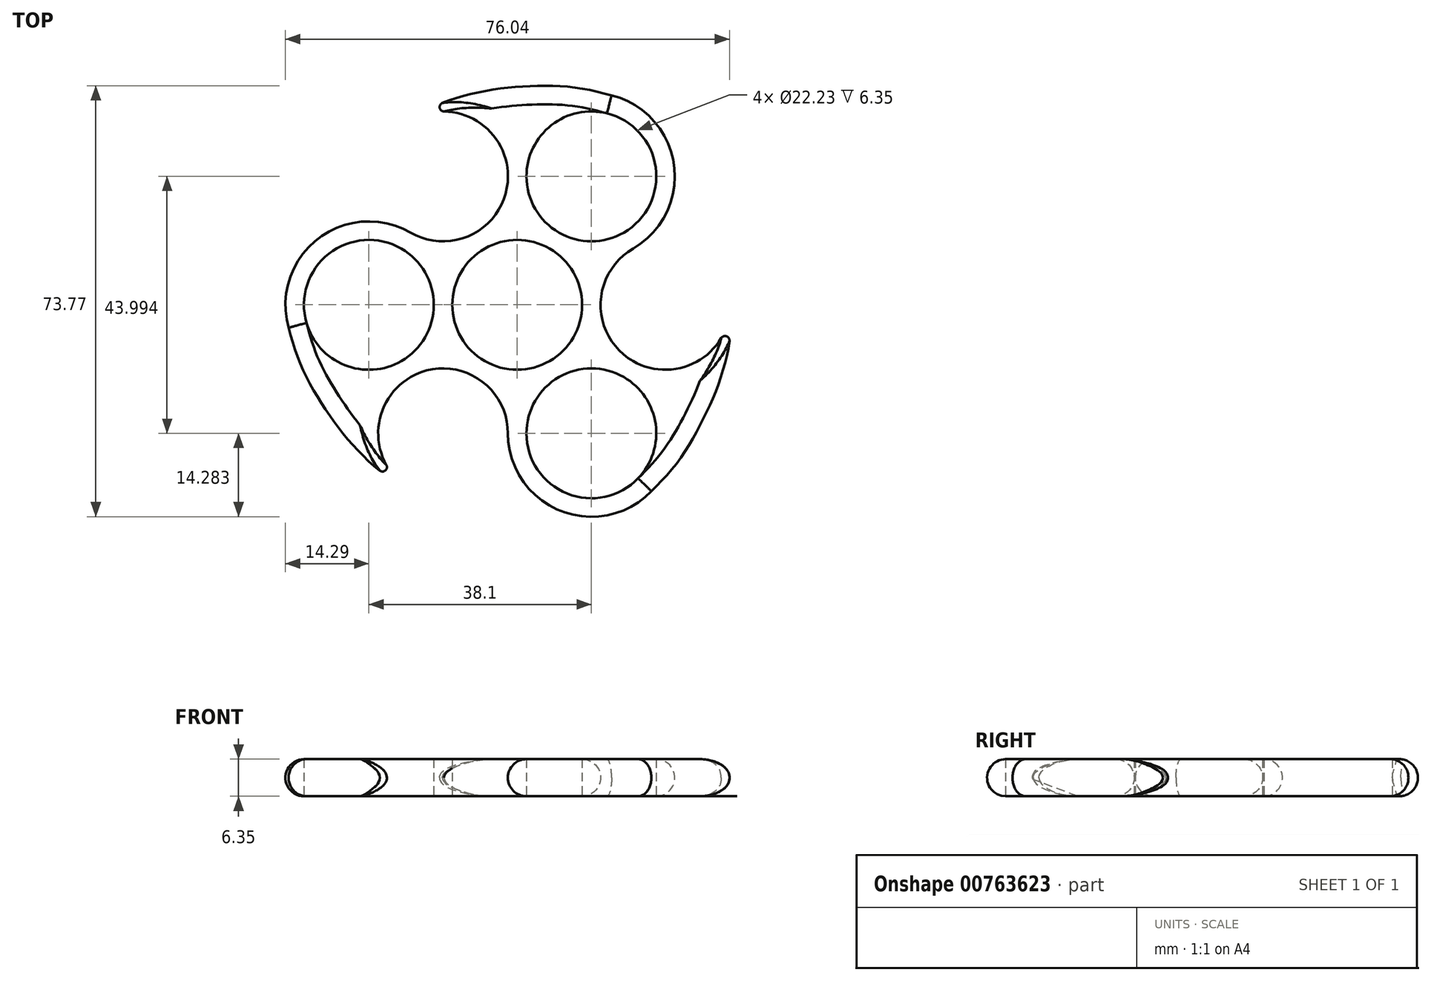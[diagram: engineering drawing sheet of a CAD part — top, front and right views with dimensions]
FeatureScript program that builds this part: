
annotation { "Feature Type Name" : "Feature", "Feature Type Description" : "" }
export const myFeature = defineFeature(function(context is Context, id is Id, definition is map)
    precondition{}
    {
        {
            var Q0;
            Q0=qCreatedBy(makeId("Top.planeOp"),FACE);
            var sketch = newSketch(context, id + "F0", { "sketchPlane" : qUnion([Q0])});
            skCircle(sketch, "E0", {"center": v(-25.4, 0) * mm, "radius": 14.29 * mm});
            skCircle(sketch, "E1.1.0", {"center": v(12.7, -22) * mm, "radius": 14.29 * mm});
            skCircle(sketch, "E1.2.0", {"center": v(12.7, 22) * mm, "radius": 14.29 * mm});
            skPoint(sketch, "E1.center", {"position": v(0, 0) * mm});
            skLineSegment(sketch, "E2", {"start": v(-7.14, 12.37) * mm, "end": v(-12.7, 22) * mm});
            skPoint(sketch, "E3", {"position": v(-12.7, 22) * mm});
            skArc(sketch, "E4", {"start": v(-18.26, 12.37) * mm, "mid": v(-7.14, 12.37) * mm, "end": v(-1.59, 22) * mm});
            skPoint(sketch, "E5", {"position": v(-11.99, 33.09) * mm});
            skFitSpline(sketch, "E6", {"points": [v(16.16, 35.86) * mm, v(10.03, 37.2) * mm, v(3.04, 37.46) * mm, v(-3.68, 36.92) * mm, v(-8.39, 35.98) * mm, v(-13.23, 34.37) * mm, v(-15.48, 32.76) * mm], "startDerivative": vector(-33.28, 8.74) * mm, "endDerivative": vector(-16.17, -13.98) * mm});
            skArc(sketch, "E7", {"start": v(-1.59, 22) * mm, "mid": v(-5.9, 30.78) * mm, "end": v(-15.48, 32.76) * mm});
            skArc(sketch, "E8.1.0", {"start": v(-18.26, -12.37) * mm, "mid": v(-23.7, -20.5) * mm, "end": v(-20.63, -29.78) * mm});
            skArc(sketch, "E8.1.1", {"start": v(-1.59, -22) * mm, "mid": v(-7.14, -12.37) * mm, "end": v(-18.26, -12.37) * mm});
            skArc(sketch, "E8.2.0", {"start": v(19.84, -9.62) * mm, "mid": v(29.6, -10.28) * mm, "end": v(36.1, -2.97) * mm});
            skArc(sketch, "E8.2.1", {"start": v(19.84, 9.62) * mm, "mid": v(14.29, 0) * mm, "end": v(19.84, -9.62) * mm});
            skFitSpline(sketch, "E9.MirrorCS", {"points": [v(22.97, -31.93) * mm, v(27.2, -27.28) * mm, v(30.92, -21.36) * mm, v(33.82, -15.27) * mm, v(35.35, -10.73) * mm, v(36.38, -5.73) * mm, v(36.1, -2.97) * mm], "startDerivative": vector(24.2, 24.45) * mm, "endDerivative": vector(-4.02, 21) * mm});
            skFitSpline(sketch, "E10.MirrorCS", {"points": [v(-39.14, -3.93) * mm, v(-37.23, -9.9) * mm, v(-33.96, -16.1) * mm, v(-30.13, -21.65) * mm, v(-26.97, -25.25) * mm, v(-23.15, -28.64) * mm, v(-20.63, -29.78) * mm], "startDerivative": vector(9.08, -33.19) * mm, "endDerivative": vector(20.2, -7.01) * mm});
            skSolve(sketch);
        }
        {
            var Q0;
            Q0 = qSketchRegion(id + "F0", true);
            extrude(context, id + "F1", {"entities" : qUnion([Q0]), "depth" : 6.35 * mm, "offsetDistance" : 25.4 * mm});
        }
        {
            var Q0;
            Q0=sQuery(id+"F0.wireOp",VERTEX,"E0.center");
            var Q1;
            Q1=sQuery(id+"F0.wireOp",VERTEX,"E1.2.0.center");
            var Q2;
            Q2=sQuery(id+"F0.wireOp",VERTEX,"E1.center");
            var Q3;
            Q3=sQuery(id+"F0.wireOp",VERTEX,"E1.1.0.center");
            var Q4;
            Q4=makeQuery(id+"F1.opExtrude","SWEPT_BODY",BODY,{"disambiguationData":[OSD([sQuery(id+"F0.wireOp",EDGE,"E0"),sQuery(id+"F0.wireOp",EDGE,"E1.1.0"),sQuery(id+"F0.wireOp",EDGE,"E1.2.0"),sQuery(id+"F0.wireOp",EDGE,"E4"),sQuery(id+"F0.wireOp",EDGE,"E6"),sQuery(id+"F0.wireOp",EDGE,"E7"),sQuery(id+"F0.wireOp",EDGE,"E8.1.0"),sQuery(id+"F0.wireOp",EDGE,"E8.1.1"),sQuery(id+"F0.wireOp",EDGE,"E8.2.0"),sQuery(id+"F0.wireOp",EDGE,"E8.2.1"),sQuery(id+"F0.wireOp",EDGE,"E9.MirrorCS"),sQuery(id+"F0.wireOp",EDGE,"E10.MirrorCS")])]});
            hole(context, id + "F2", {"style" : HoleStyle.SIMPLE, "endStyle" : HoleEndStyle.THROUGH, "oppositeDirection" : true, "holeDiameter" : 22.22 * mm, "majorDiameter" : 6.35 * mm, "isTappedThrough" : true, "tappedDepth" : 12.7 * mm, "tapClearance" : 3, "locations" : qUnion([Q0, Q1, Q2, Q3]), "scope" : qUnion([Q4])});
        }
        {
            var Q0;
            Q0=makeQuery(id+"F1.opExtrude","CAP_EDGE",EDGE,{"disambiguationData":[OSD([sQuery(id+"F0.wireOp",EDGE,"E10.MirrorCS")])],"isStart":false});
            var Q1;
            Q1=makeQuery(id+"F1.opExtrude","CAP_EDGE",EDGE,{"disambiguationData":[OSD([sQuery(id+"F0.wireOp",EDGE,"E0")])],"isStart":false});
            var Q2;
            Q2=makeQuery(id+"F1.opExtrude","CAP_EDGE",EDGE,{"disambiguationData":[OSD([sQuery(id+"F0.wireOp",EDGE,"E6")])],"isStart":false});
            var Q3;
            Q3=makeQuery(id+"F1.opExtrude","CAP_EDGE",EDGE,{"disambiguationData":[OSD([sQuery(id+"F0.wireOp",EDGE,"E1.2.0")])],"isStart":false});
            var Q4;
            Q4=makeQuery(id+"F1.opExtrude","CAP_EDGE",EDGE,{"disambiguationData":[OSD([sQuery(id+"F0.wireOp",EDGE,"E9.MirrorCS")])],"isStart":false});
            var Q5;
            Q5=makeQuery(id+"F1.opExtrude","CAP_EDGE",EDGE,{"disambiguationData":[OSD([sQuery(id+"F0.wireOp",EDGE,"E1.1.0")])],"isStart":false});
            var Q6;
            Q6=makeQuery(id+"F1.opExtrude","CAP_EDGE",EDGE,{"disambiguationData":[OSD([sQuery(id+"F0.wireOp",EDGE,"E10.MirrorCS")])],"isStart":true});
            var Q7;
            Q7=makeQuery(id+"F1.opExtrude","CAP_EDGE",EDGE,{"disambiguationData":[OSD([sQuery(id+"F0.wireOp",EDGE,"E0")])],"isStart":true});
            var Q8;
            Q8=makeQuery(id+"F1.opExtrude","CAP_EDGE",EDGE,{"disambiguationData":[OSD([sQuery(id+"F0.wireOp",EDGE,"E6")])],"isStart":true});
            var Q9;
            Q9=makeQuery(id+"F1.opExtrude","CAP_EDGE",EDGE,{"disambiguationData":[OSD([sQuery(id+"F0.wireOp",EDGE,"E1.2.0")])],"isStart":true});
            var Q10;
            Q10=makeQuery(id+"F1.opExtrude","CAP_EDGE",EDGE,{"disambiguationData":[OSD([sQuery(id+"F0.wireOp",EDGE,"E9.MirrorCS")])],"isStart":true});
            var Q11;
            Q11=makeQuery(id+"F1.opExtrude","CAP_EDGE",EDGE,{"disambiguationData":[OSD([sQuery(id+"F0.wireOp",EDGE,"E1.1.0")])],"isStart":true});
            fillet(context, id + "F3", {"entities" : qUnion([Q0, Q1, Q2, Q3, Q4, Q5, Q6, Q7, Q8, Q9, Q10, Q11]), "radius" : 3.17 * mm, "tangentPropagation" : true, "allowEdgeOverflow" : false});
        }
        {
            var Q0;
            Q0=makeQuery(id+"F3.opFillet","BLEND_EDGE",EDGE,{"blendedFrom":[makeQuery(id+"F1.opExtrude","CAP_EDGE",EDGE,{"disambiguationData":[OSD([sQuery(id+"F0.wireOp",EDGE,"E8.2.0")])],"isStart":false}),makeQuery(id+"F1.opExtrude","CAP_EDGE",EDGE,{"disambiguationData":[OSD([sQuery(id+"F0.wireOp",EDGE,"E9.MirrorCS")])],"isStart":false})],"blendedInto":[]});
            var Q1;
            Q1=makeQuery(id+"F3.opFillet","BLEND_EDGE",EDGE,{"blendedFrom":[makeQuery(id+"F1.opExtrude","CAP_EDGE",EDGE,{"disambiguationData":[OSD([sQuery(id+"F0.wireOp",EDGE,"E6")])],"isStart":true}),makeQuery(id+"F1.opExtrude","CAP_EDGE",EDGE,{"disambiguationData":[OSD([sQuery(id+"F0.wireOp",EDGE,"E7")])],"isStart":true})],"blendedInto":[]});
            var Q2;
            Q2=makeQuery(id+"F3.opFillet","BLEND_EDGE",EDGE,{"blendedFrom":[makeQuery(id+"F1.opExtrude","CAP_EDGE",EDGE,{"disambiguationData":[OSD([sQuery(id+"F0.wireOp",EDGE,"E8.1.0")])],"isStart":false}),makeQuery(id+"F1.opExtrude","CAP_EDGE",EDGE,{"disambiguationData":[OSD([sQuery(id+"F0.wireOp",EDGE,"E10.MirrorCS")])],"isStart":false})],"blendedInto":[]});
            var Q3;
            Q3=makeQuery(id+"F2.hole-2.boolean.opBoolean","INTERSECT",EDGE,{"derivedFrom":[makeQuery(id+"F1.opExtrude","CAP_FACE",FACE,{"disambiguationData":[OSD([sQuery(id+"F0.wireOp",EDGE,"E0"),sQuery(id+"F0.wireOp",EDGE,"E1.1.0"),sQuery(id+"F0.wireOp",EDGE,"E1.2.0"),sQuery(id+"F0.wireOp",EDGE,"E4"),sQuery(id+"F0.wireOp",EDGE,"E6"),sQuery(id+"F0.wireOp",EDGE,"E7"),sQuery(id+"F0.wireOp",EDGE,"E8.1.0"),sQuery(id+"F0.wireOp",EDGE,"E8.1.1"),sQuery(id+"F0.wireOp",EDGE,"E8.2.0"),sQuery(id+"F0.wireOp",EDGE,"E8.2.1"),sQuery(id+"F0.wireOp",EDGE,"E9.MirrorCS"),sQuery(id+"F0.wireOp",EDGE,"E10.MirrorCS")])],"isStart":false}),makeQuery(id+"F2.hole-2.opRevolve","SWEPT_FACE",FACE,{"disambiguationData":[OSD([sQuery(id+"F2.hole-2.sketch.wireOp",EDGE,"core_line_2")])]})]});
            var Q4;
            Q4=makeQuery(id+"F2.hole-2.boolean.opBoolean","COPY",EDGE,{"derivedFrom":makeQuery(id+"F2.hole-2.opRevolve","SWEPT_EDGE",EDGE,{"disambiguationData":[OSD([sQuery(id+"F2.hole-2.sketch.wireOp",EDGE,"core_line_2"),sQuery(id+"F2.hole-2.sketch.wireOp",EDGE,"core_line_3")])]})});
            fillet(context, id + "F4", {"entities" : qUnion([Q0, Q1, Q2, Q3, Q4]), "radius" : 0.76 * mm, "tangentPropagation" : true, "allowEdgeOverflow" : false});
        }
    });
